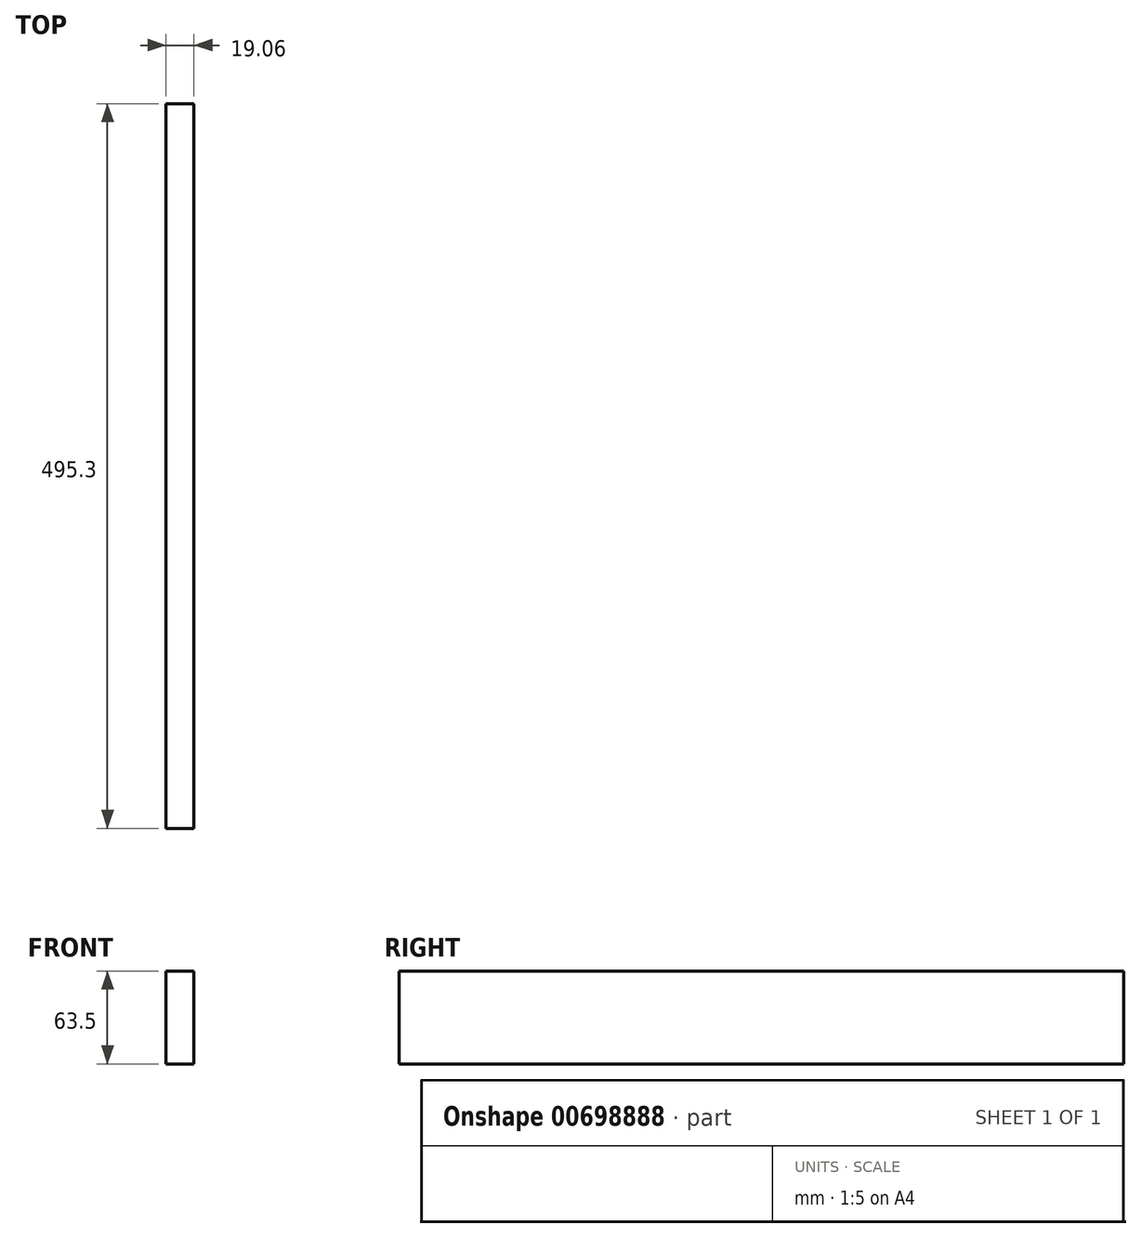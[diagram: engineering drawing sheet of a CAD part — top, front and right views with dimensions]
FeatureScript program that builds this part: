
annotation { "Feature Type Name" : "Feature", "Feature Type Description" : "" }
export const myFeature = defineFeature(function(context is Context, id is Id, definition is map)
    precondition{}
    {
        {
            var Q0;
            Q0=qCreatedBy(makeId("Right.planeOp"),FACE);
            var sketch = newSketch(context, id + "F0", { "sketchPlane" : qUnion([Q0])});
            skLineSegment(sketch, "E0.bottom", {"start": v(247.65, 31.75) * mm, "end": v(-247.65, 31.75) * mm});
            skLineSegment(sketch, "E0.top", {"start": v(247.65, -31.75) * mm, "end": v(-247.65, -31.75) * mm});
            skLineSegment(sketch, "E0.left", {"start": v(247.65, 31.75) * mm, "end": v(247.65, -31.75) * mm});
            skLineSegment(sketch, "E0.right", {"start": v(-247.65, 31.75) * mm, "end": v(-247.65, -31.75) * mm});
            skPoint(sketch, "E0.middle", {"position": v(0, 0) * mm});
            skSolve(sketch);
        }
        {
            var Q0;
            Q0 = qSketchRegion(id + "F0", true);
            extrude(context, id + "F1", {"entities" : qUnion([Q0]), "endBound" : BoundingType.SYMMETRIC, "depth" : 19.05 * mm, "offsetDistance" : 25.4 * mm});
        }
    });
